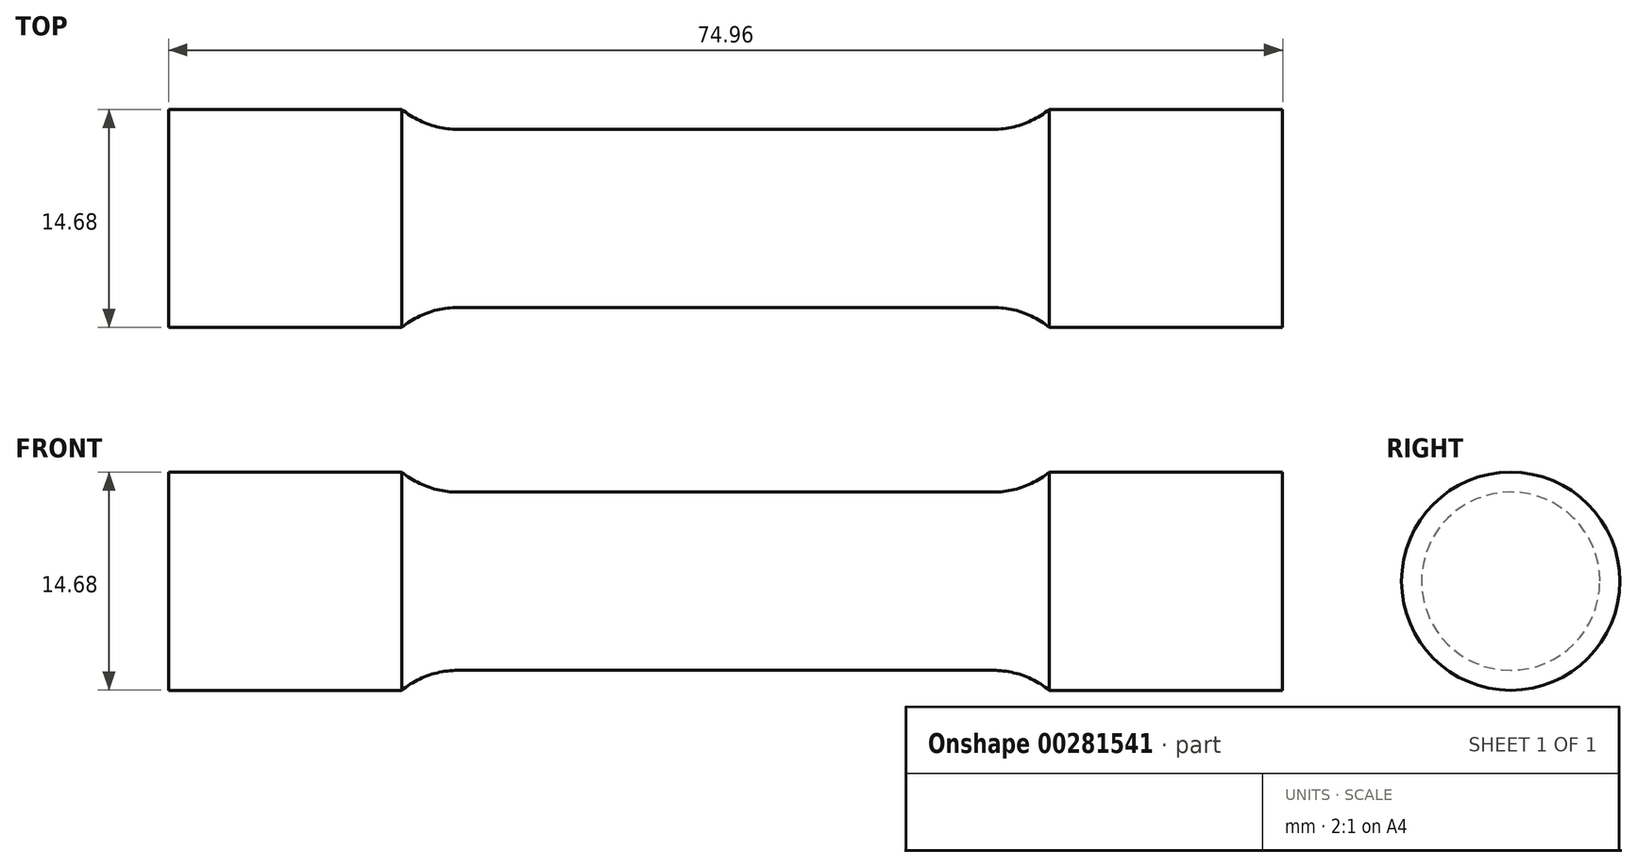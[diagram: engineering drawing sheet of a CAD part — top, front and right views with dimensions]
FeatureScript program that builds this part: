
annotation { "Feature Type Name" : "Feature", "Feature Type Description" : "" }
export const myFeature = defineFeature(function(context is Context, id is Id, definition is map)
    precondition{}
    {
        {
            var Q0;
            Q0=qCreatedBy(makeId("Front.planeOp"),FACE);
            var sketch = newSketch(context, id + "F0", { "sketchPlane" : qUnion([Q0])});
            skLineSegment(sketch, "E0", {"start": v(0, 6) * mm, "end": v(18, 6) * mm});
            skArc(sketch, "E1", {"start": v(18, 6) * mm, "mid": v(20, 6.35) * mm, "end": v(21.78, 7.34) * mm});
            skLineSegment(sketch, "E2", {"start": v(21.78, 7.34) * mm, "end": v(37.48, 7.34) * mm});
            skLineSegment(sketch, "E3", {"start": v(37.48, 7.34) * mm, "end": v(37.48, 0) * mm});
            skLineSegment(sketch, "E4.MirrorCS", {"start": v(0, 6) * mm, "end": v(-18, 6) * mm});
            skLineSegment(sketch, "E5.MirrorCS", {"start": v(-37.48, 7.34) * mm, "end": v(-37.48, 0) * mm});
            skLineSegment(sketch, "E6.MirrorCS", {"start": v(-21.78, 7.34) * mm, "end": v(-37.48, 7.34) * mm});
            skArc(sketch, "E7.MirrorCS", {"start": v(-18, 6) * mm, "mid": v(-20, 6.35) * mm, "end": v(-21.78, 7.34) * mm});
            skLineSegment(sketch, "E8", {"start": v(-37.48, 0) * mm, "end": v(37.48, 0) * mm});
            skSolve(sketch);
        }
        {
            var Q0;
            Q0 = qSketchRegion(id + "F0", true);
            var Q1;
            Q1=sQuery(id+"F0.wireOp",EDGE,"E8");
            revolve(context, id + "F1", {"entities" : qUnion([Q0]), "axis" : qUnion([Q1]), "revolveType" : RevolveType.FULL});
        }
    });
